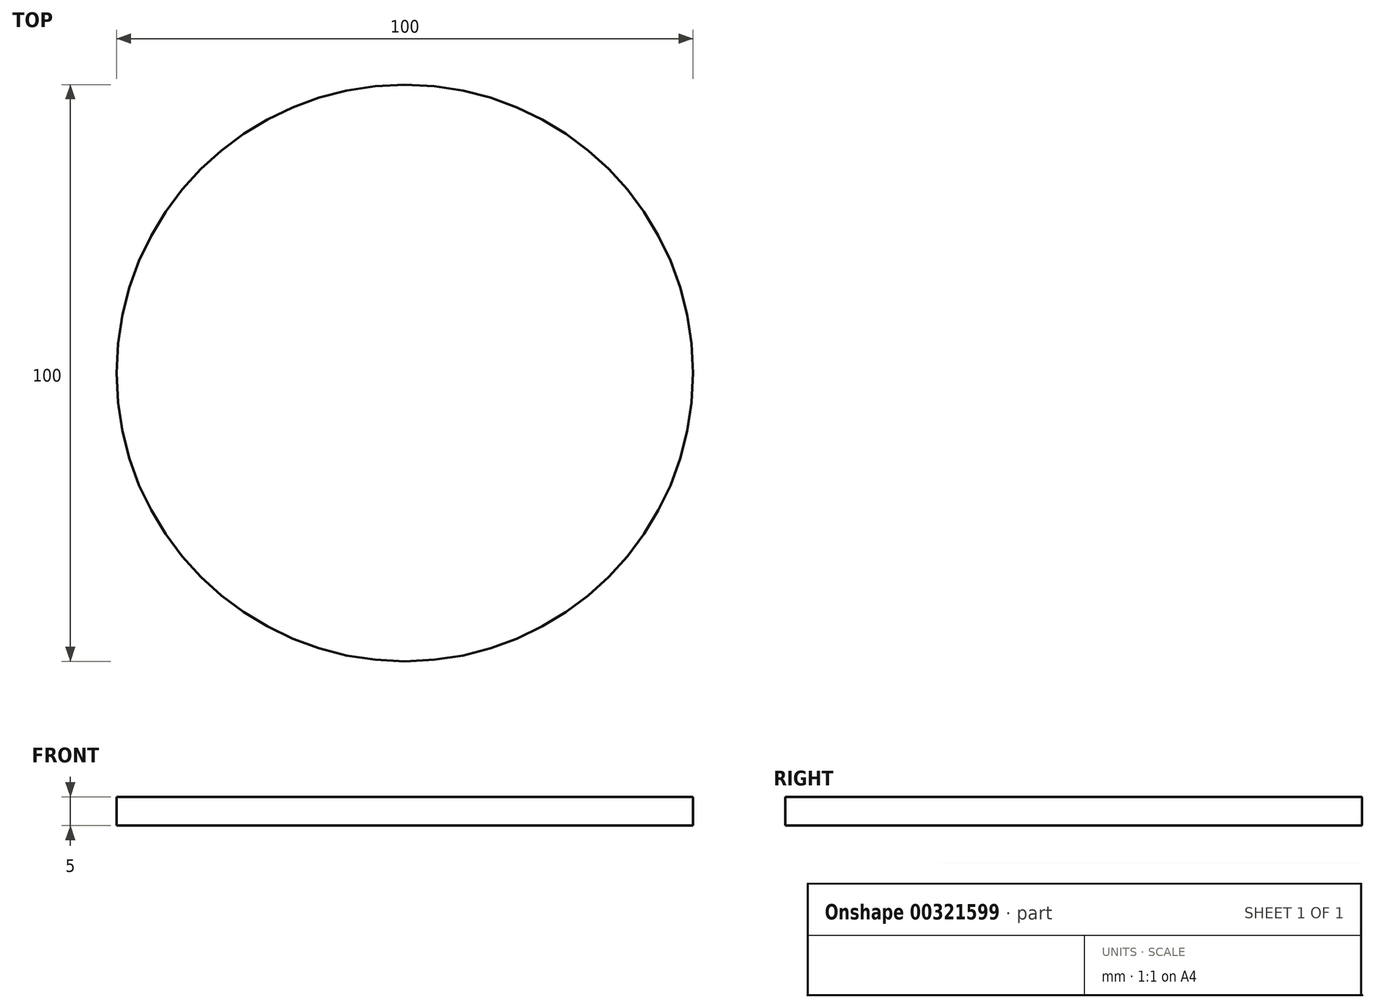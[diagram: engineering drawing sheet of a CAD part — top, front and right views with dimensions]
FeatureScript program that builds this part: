
annotation { "Feature Type Name" : "Feature", "Feature Type Description" : "" }
export const myFeature = defineFeature(function(context is Context, id is Id, definition is map)
    precondition{}
    {
        {
            var Q0;
            Q0=qCreatedBy(makeId("Top.planeOp"),FACE);
            var sketch = newSketch(context, id + "F0", { "sketchPlane" : qUnion([Q0])});
            skCircle(sketch, "E0", {"center": v(0, 0) * mm, "radius": 50 * mm});
            skSolve(sketch);
        }
        {
            var Q0;
            Q0=makeQuery(id+"F0.imprint","IMPRINT",FACE,{"disambiguationData":[TD([[makeQuery(id+"F0.imprint","IMPRINT",EDGE,{"derivedFrom":sQuery(id+"F0.wireOp",EDGE,"E0")}),1.0]])]});
            extrude(context, id + "F1", {"entities" : qUnion([Q0]), "depth" : 5 * mm});
        }
    });
